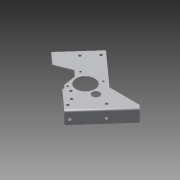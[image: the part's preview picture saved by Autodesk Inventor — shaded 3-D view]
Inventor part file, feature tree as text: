
AUTODESK INVENTOR PART (.ipt)
format: ipt  version: 2013 (Build 170138000, 138)  size: 553,984 bytes
history: native  units: in
note: dims shown in document units (in); Inventor stores cm internally (conversion verified against a paired STEP export)
features: sheet_metal_op x33, other x27, sketch x26, reference x1, extrude x1
ambient origin geometry x8: Origin, YZ Plane, XZ Plane, XY Plane, X Axis, Y Axis, Z Axis, Center Point
feature tree (88):
  sheet_metal_op  "Face2"
  sheet_metal_op  "Face5"
  sheet_metal_op  "Face6"
  sheet_metal_op  "Face7"
  sheet_metal_op  "Flange4"
  sheet_metal_op  "Flange5"
  sheet_metal_op  "Face8"
  sheet_metal_op  "Face9"
  sheet_metal_op  "Flange6"
  sheet_metal_op  "Flange7"
  sheet_metal_op  "Face10"
  sheet_metal_op  "Flange8"
  sheet_metal_op  "Flange9"
  sheet_metal_op  "Face13"
  sketch  "Sketch1"  dims[d8=0.125in]
  other  "Plate3"
  sketch  "Sketch8"  dims[d19=1.875in d20=0.375in d21=0.375in d22=0.375in d23=1.125in d24=1.6742in d25=1.6742in d26=1.8904in d27=0.3in d28=0.3in d29=0.3in d30=0.3in d31=0.125in]
  sketch  "Sketch9"  dims[d32=1.0in]
  other  "Plate8"
  sheet_metal_op  "Bend6"
  sketch  "Sketch10"  dims[d33=1.25in]
  sketch  "Sketch11"  dims[d86=2.0in]
  other  "Plate9"
  sheet_metal_op  "Bend7"
  sketch  "Sketch12"  dims[d87=0.125in]
  sketch  "Sketch14"  dims[d88=0.0in]
  sketch  "Sketch15"  dims[d89=3.0in]
  other  "Plate10"
  sheet_metal_op  "Bend8"
  sketch  "Sketch16"  dims[d90=0.125in]
  other  "Plate11"
  sheet_metal_op  "Bend9"
  sheet_metal_op  "Corner4"
  sketch  "Sketch17"  dims[d91=0.125in]
  other  "Plate12"
  sheet_metal_op  "Bend10"
  sheet_metal_op  "Corner5"
  sketch  "Sketch18"  dims[d92=0.0625in]
  sketch  "Sketch19"  dims[d93=0.25in]
  sketch  "Sketch20"  dims[d94=0.125in]
  reference  "Reference4"
  sketch  "Sketch21"  dims[d95=0.266in]
  sketch  "Sketch22"  dims[d96=0.266in]
  sketch  "Sketch23"  dims[d97=2.75in]
  other  "Plate13"
  sheet_metal_op  "Bend11"
  sketch  "Sketch24"  dims[d98=0.3125in]
  sketch  "Sketch25"  dims[d99=0.5in]
  sketch  "Sketch26"  dims[d100=0.5in]
  other  "Plate14"
  sheet_metal_op  "Bend12"
  sketch  "Sketch27"  dims[d101=0.125in]
  other  "Plate15"
  sheet_metal_op  "Bend13"
  sheet_metal_op  "Corner6"
  sketch  "Sketch28"  dims[d102=0.0in]
  other  "Plate16"
  sheet_metal_op  "Bend14"
  sheet_metal_op  "Corner7"
  sketch  "Sketch29"  dims[d103=3.875in]
  other  "Plate17"
  sheet_metal_op  "Bend15"
  sketch  "Sketch30"  dims[d104=2.375in]
  other  "Plate18"
  sheet_metal_op  "Bend16"
  sheet_metal_op  "Corner8"
  sketch  "Sketch31"  dims[d105=0.125in]
  other  "Plate19"
  sheet_metal_op  "Bend17"
  sheet_metal_op  "Corner9"
  sketch  "Sketch38"  dims[d106=0.125in]
  sketch  "Sketch39"  dims[d107=0.0625in d108=0.25in d109=0.125in d110=0.266in d111=0.266in d112=0.5in d113=0.375in d114=1.5in d115=0.5in d116=0.125in d117=0.0in d124=0.0625in d126=0.125in d127=0.0in d128=0.2in d130=0.2in d131=0.2in d132=0.125in d133=0.125in d134=0.0625in d135=0.25in d136=0.125in d137=0.125in d138=0.0625in d139=0.25in d140=0.125in d141=1.25in d142=90.0deg d143=0.05in d144=0.5in d145=0.125in d146=0.125in d147=0.125in d148=0.0625in d149=0.25in d150=0.125in d151=1.25in d152=90.0deg d153=0.05in d154=0.5in d155=0.125in d156=0.125in d157=0.266in d158=0.266in d159=0.5in d160=0.375in d161=0.375in d162=0.5in d163=100.0in d164=0.0in d165=0.266in d166=0.375in d167=0.5in d168=0.125in d169=0.0in d171=0.748in d172=1.0in d173=24.0in d174=0.125in d175=0.0in d176=1.75in d177=0.5in d178=1.0in d179=0.266in d180=0.266in d181=0.125in d182=0.0in d183=0.2in d184=0.0687in d186=1.2992in d187=1.2992in d188=0.2in d189=0.0687in d190=1.2992in d191=1.2992in d192=0.2in d193=0.0687in d194=1.5154in d195=1.5154in d196=0.125in d197=0.0in d198=0.125in d199=0.125in d200=0.0625in d201=0.25in d202=0.125in d203=2.5in d204=0.125in d205=0.0in d206=0.25in d207=0.125in d208=0.0in d209=1.5in d210=2.25in d211=0.125in d212=0.125in d213=0.0625in d214=0.25in d215=0.125in d216=1.5in d217=0.125in d218=0.0625in d219=0.25in d220=0.125in d221=1.25in d222=90.0deg d223=0.05in d224=0.5in d225=0.125in d226=0.125in d227=0.125in d228=0.0625in d229=0.25in d230=0.125in d231=1.25in d232=90.0deg d233=0.05in d234=0.5in d235=0.125in d236=0.125in d237=2.0in d238=0.25in d239=2.5in d240=0.125in d241=0.125in d242=0.0625in d243=0.25in d244=0.125in d245=0.125in d246=0.0625in d247=0.25in d248=0.125in d249=1.25in d250=90.0deg d251=0.05in d252=0.5in d253=0.125in d254=0.125in d255=0.125in d256=0.0625in d257=0.25in d258=0.125in d259=1.25in d260=90.0deg d261=0.05in d262=0.5in d263=0.125in d264=0.125in d270=90.0deg d272=0.375in d302=0.266in d303=0.266in d304=1.0in d305=0.25in d306=0.125in d307=0.0in d308=0.125in d309=0.125in d310=0.0625in d311=0.25in d312=0.125in d0=0.125in d1=0.0625in d2=0.25in d3=0.125in d5=0.125in d6=0.0625in d7=0.25in d9=0.0in d10=0.125in d11=0.0625in d12=0.25in d13=0.125in d14=0.25in d15=0.125in d16=0.0625in d17=0.125in d18=1.0in]
  other  "Plate22"
  sheet_metal_op  "Bend20"
  other  "Cut2"
  other  "Cut3"
  other  "Cut4"
  other  "Cut6"
  other  "Cut7"
  other  "Cut8"
  other  "Cut9"
  other  "Cut10"
  other  "Cut11"
  other  "Cut12"
  other  "Cut13"
  other  "Cut18"
  other  "Definition1"
  extrude  "Extrusion1"  Depth=0.125in
